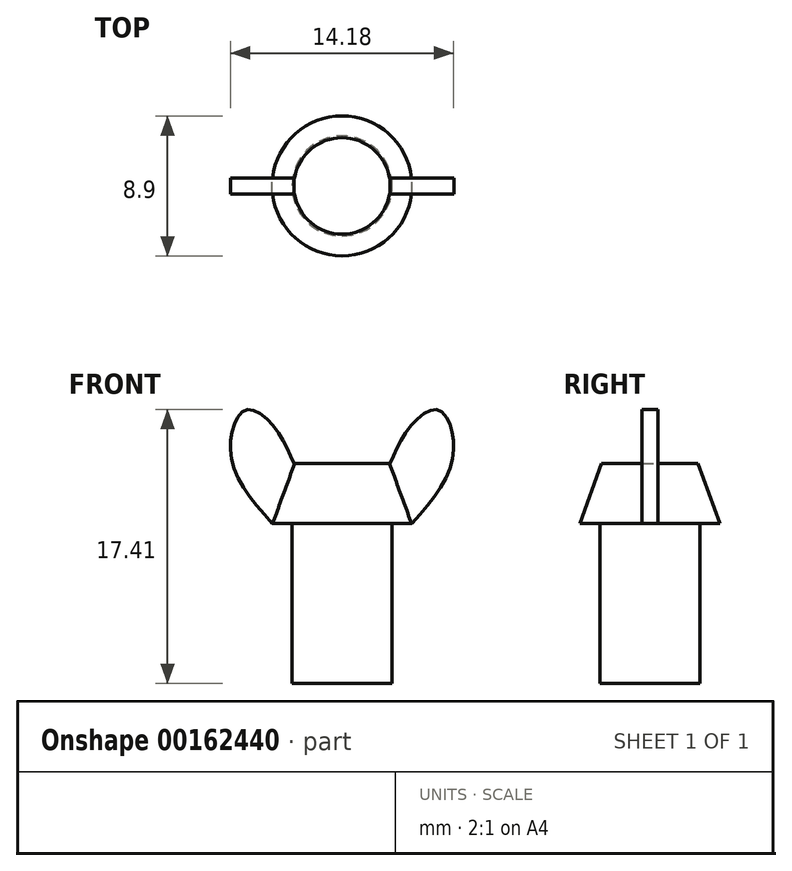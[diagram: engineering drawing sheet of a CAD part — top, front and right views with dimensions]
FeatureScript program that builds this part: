
annotation { "Feature Type Name" : "Feature", "Feature Type Description" : "" }
export const myFeature = defineFeature(function(context is Context, id is Id, definition is map)
    precondition{}
    {
        {
            var Q0;
            Q0=qCreatedBy(makeId("Top.planeOp"),FACE);
            var sketch = newSketch(context, id + "F0", { "sketchPlane" : qUnion([Q0])});
            skCircle(sketch, "E0", {"center": v(0, 0) * mm, "radius": 3.18 * mm});
            skSolve(sketch);
        }
        {
            var Q0;
            Q0 = qSketchRegion(id + "F0", true);
            extrude(context, id + "F1", {"entities" : qUnion([Q0]), "depth" : 7.62 * mm, "hasSecondDirection" : true, "secondDirectionOppositeDirection" : true, "secondDirectionDepth" : 2.54 * mm});
        }
        {
            var Q0;
            Q0=makeQuery(id+"F1.opExtrude","CAP_FACE",FACE,{"disambiguationData":[OSD([sQuery(id+"F0.wireOp",EDGE,"E0")])],"isStart":false});
            var sketch = newSketch(context, id + "F2", { "sketchPlane" : qUnion([Q0])});
            skCircle(sketch, "E1", {"center": v(0, 0) * mm, "radius": 4.45 * mm});
            skSolve(sketch);
        }
        {
            var Q0;
            Q0 = qSketchRegion(id + "F2", true);
            extrude(context, id + "F3", {"entities" : qUnion([Q0]), "operationType" : NewBodyOperationType.ADD, "depth" : 3.8 * mm, "hasDraft" : true, "draftAngle" : 20 * degree, "draftPullDirection" : true});
        }
        {
            var Q0;
            Q0=qCreatedBy(makeId("Front.planeOp"),FACE);
            var sketch = newSketch(context, id + "F4", { "sketchPlane" : qUnion([Q0])});
            skLineSegment(sketch, "E2.0", {"start": v(-4.45, 7.62) * mm, "end": v(4.45, 7.62) * mm, "construction": true});
            skLineSegment(sketch, "E3.0", {"start": v(-3.06, 11.43) * mm, "end": v(3.06, 11.43) * mm, "construction": true});
            skFitSpline(sketch, "E4", {"points": [v(-4.45, 7.62) * mm, v(-6.84, 11.1) * mm, v(-6.89, 13.83) * mm, v(-5.94, 14.87) * mm, v(-4.24, 13.67) * mm, v(-3.06, 11.43) * mm], "startDerivative": vector(-11.41, 13.2) * mm, "endDerivative": vector(4.75, -11.46) * mm});
            skFitSpline(sketch, "E5.MirrorCS", {"points": [v(4.45, 7.62) * mm, v(6.84, 11.1) * mm, v(6.89, 13.83) * mm, v(5.94, 14.87) * mm, v(4.24, 13.67) * mm, v(3.06, 11.43) * mm], "startDerivative": vector(11.41, 13.2) * mm, "endDerivative": vector(-4.75, -11.46) * mm});
            skLineSegment(sketch, "E6.0", {"start": v(-4.3, 7.62) * mm, "end": v(-2.92, 11.43) * mm});
            skLineSegment(sketch, "E7", {"start": v(-2.92, 11.43) * mm, "end": v(-3.06, 11.43) * mm});
            skLineSegment(sketch, "E8", {"start": v(-4.3, 7.62) * mm, "end": v(-4.45, 7.62) * mm});
            skLineSegment(sketch, "E9.0", {"start": v(2.92, 11.43) * mm, "end": v(4.3, 7.62) * mm});
            skLineSegment(sketch, "E10", {"start": v(4.3, 7.62) * mm, "end": v(4.45, 7.62) * mm});
            skLineSegment(sketch, "E11", {"start": v(2.92, 11.43) * mm, "end": v(3.06, 11.43) * mm});
            skSolve(sketch);
        }
        {
            var Q0;
            Q0 = qSketchRegion(id + "F4", true);
            extrude(context, id + "F5", {"entities" : qUnion([Q0]), "operationType" : NewBodyOperationType.ADD, "depth" : 0.5 * mm, "hasSecondDirection" : true, "secondDirectionOppositeDirection" : true, "secondDirectionDepth" : 0.5 * mm});
        }
    });
